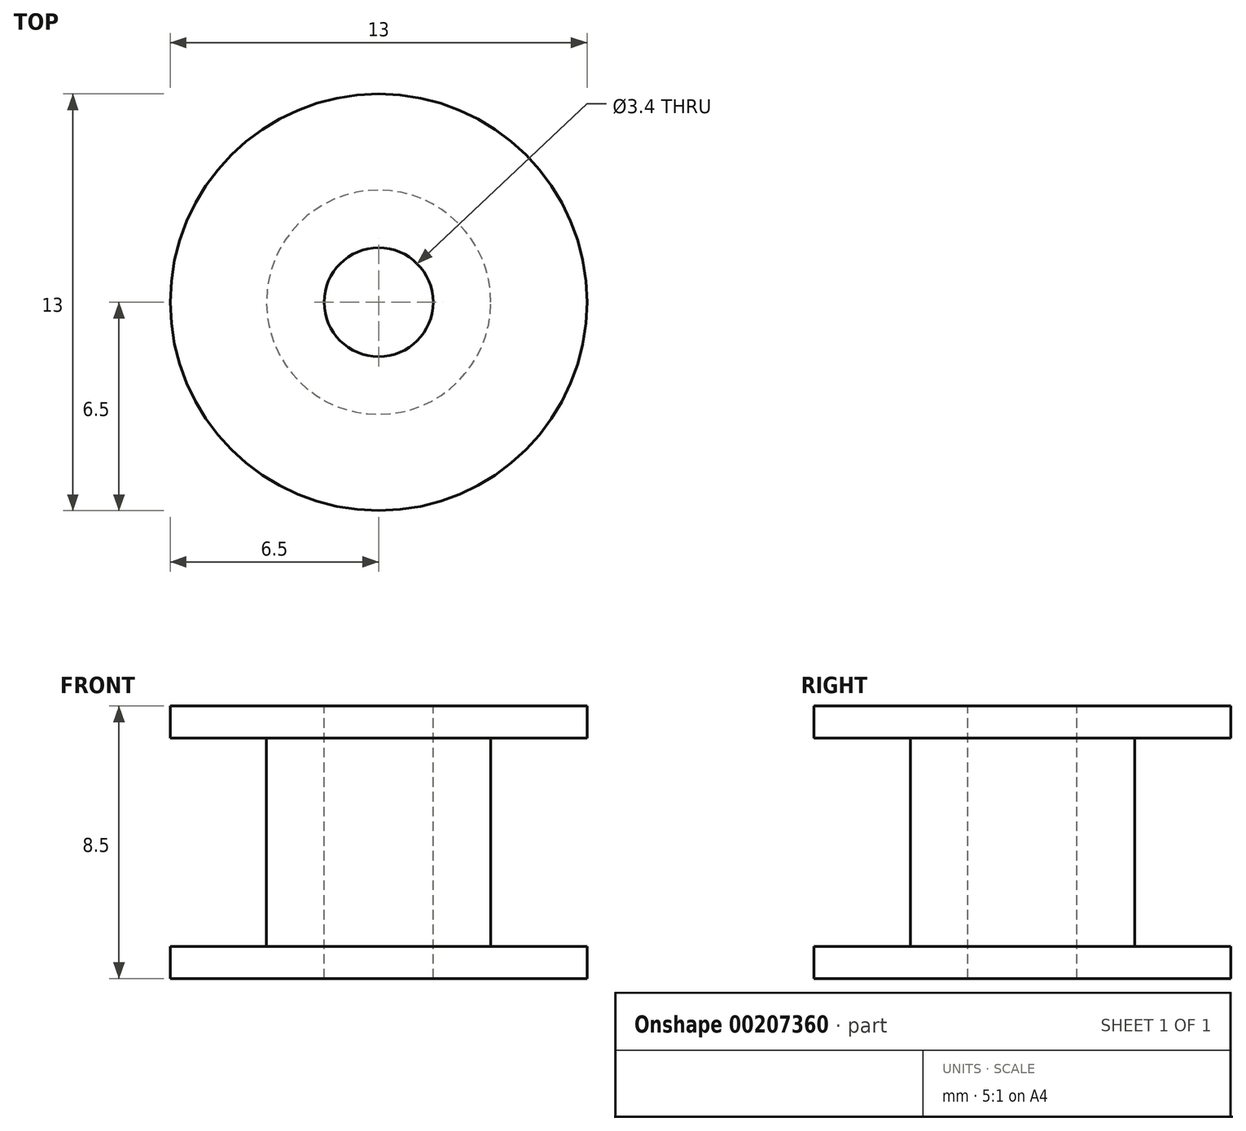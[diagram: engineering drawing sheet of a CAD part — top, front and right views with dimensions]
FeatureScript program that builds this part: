
annotation { "Feature Type Name" : "Feature", "Feature Type Description" : "" }
export const myFeature = defineFeature(function(context is Context, id is Id, definition is map)
    precondition{}
    {
        {
            var Q0;
            Q0=qCreatedBy(makeId("Top.planeOp"),FACE);
            var sketch = newSketch(context, id + "F0", { "sketchPlane" : qUnion([Q0])});
            skCircle(sketch, "E0", {"center": v(0, 0) * mm, "radius": 6.5 * mm});
            skCircle(sketch, "E1", {"center": v(0, 0) * mm, "radius": 3.5 * mm});
            skSolve(sketch);
        }
        {
            var Q0;
            Q0=makeQuery(id+"F0.imprint","IMPRINT",FACE,{"disambiguationData":[TD([[makeQuery(id+"F0.imprint","IMPRINT",EDGE,{"derivedFrom":sQuery(id+"F0.wireOp",EDGE,"E1")}),1.0]])]});
            var Q1;
            Q1=makeQuery(id+"F0.imprint","IMPRINT",FACE,{"disambiguationData":[TD([[makeQuery(id+"F0.imprint","IMPRINT",EDGE,{"derivedFrom":sQuery(id+"F0.wireOp",EDGE,"E0")}),1.0]])]});
            extrude(context, id + "F1", {"entities" : qUnion([Q0, Q1]), "depth" : 1 * mm, "offsetDistance" : 25 * mm});
        }
        {
            var Q0;
            Q0=makeQuery(id+"F0.imprint","IMPRINT",FACE,{"disambiguationData":[TD([[makeQuery(id+"F0.imprint","IMPRINT",EDGE,{"derivedFrom":sQuery(id+"F0.wireOp",EDGE,"E1")}),1.0]])]});
            var Q1;
            Q1=sQuery(id+"F0.wireOp",EDGE,"E1");
            extrude(context, id + "F2", {"entities" : qUnion([Q0]), "operationType" : NewBodyOperationType.ADD, "surfaceOperationType" : NewSurfaceOperationType.ADD, "surfaceEntities" : qUnion([Q1]), "depth" : (8.5 / 2) * mm, "offsetDistance" : 25 * mm});
        }
        {
            var Q0;
            Q0=makeQuery(id+"F1.opExtrude","SWEPT_BODY",BODY,{"disambiguationData":[OSD([sQuery(id+"F0.wireOp",EDGE,"E0")])]});
            var Q1;
            Q1=makeQuery(id+"F2.opExtrude","CAP_FACE",FACE,{"disambiguationData":[OSD([sQuery(id+"F0.wireOp",EDGE,"E1")])],"isStart":false});
            mirror(context, id + "F3", {"operationType" : NewBodyOperationType.ADD, "entities" : qUnion([Q0]), "mirrorPlane" : qUnion([Q1])});
        }
        {
            var Q0;
            Q0=sQuery(id+"F0.wireOp",VERTEX,"E0.center");
            var Q1;
            Q1=makeQuery(id+"F1.opExtrude","SWEPT_BODY",BODY,{"disambiguationData":[OSD([sQuery(id+"F0.wireOp",EDGE,"E0")])]});
            hole(context, id + "F4", {"style" : HoleStyle.SIMPLE, "endStyle" : HoleEndStyle.THROUGH, "oppositeDirection" : true, "standardTappedOrClearance" : lookupTablePath({ "fit" : "Normal", "standard" : "ISO", "size" : "M3", "type" : "Clearance" }), "standardBlindInLast" : lookupTablePath({ "fit" : "Normal", "standard" : "ISO", "engagement" : "75%", "pitch" : "0.5 mm", "size" : "M3", "type" : "Clearance & tapped" }), "holeDiameter" : 3.4 * mm, "majorDiameter" : 5 * mm, "isTappedThrough" : true, "tappedDepth" : 12 * mm, "tapClearance" : 3, "locations" : qUnion([Q0]), "scope" : qUnion([Q1]), "startStyle" : HoleStartStyle.SKETCH});
        }
    });
